FCSTD DOCUMENT  (FreeCAD 0.20R29603 (Git))
Label: NombresBoda
License: All rights reserved
LicenseURL: http://en.wikipedia.org/wiki/All_rights_reserved
objects: Part::Part2DObjectPython×37, Part::Extrusion×37, App::DocumentObjectGroup×26, Part::MultiFuse×25, Part::Box×17, Part::Fuse×3
note: 119 computed .brp shape members not serialized (recipe doc carries the construction recipe); baked Part::Feature solids carry a one-line shape summary decoded from their .brp

FEATURE [Part::Part2DObjectPython] ShapeString  # Draft 2D object (typed FeaturePython)
  FontFile = <userpath>/Desktop/Pacifico/Pacifico-Regular.ttf
  MakeFace = true
  Placement = pos=(11.57,0.12,0) rot=(0,0,1;0rad)
  Size = 16
  String = uli
  Tracking = 0
FEATURE [Part::Part2DObjectPython] ShapeString001  # Draft 2D object (typed FeaturePython)
  FontFile = <userpath>/Desktop/Pacifico/Pacifico-Regular.ttf
  MakeFace = true
  Placement = pos=(-4,0.7,0) rot=(0,0,1;0rad)
  Size = 16
  String = J
  Tracking = 0
FEATURE [Part::Extrusion] Extrude
  Base = -> ShapeString001
  Dir = (0,0,1)
  DirMode = 2
  FaceMakerClass = Part::FaceMakerBullseye
  LengthFwd = 3.5
  LengthRev = 0
  Solid = true
  Symmetric = false
FEATURE [Part::Extrusion] Extrude001
  Base = -> ShapeString
  Dir = (0,0,1)
  DirMode = 2
  FaceMakerClass = Part::FaceMakerBullseye
  LengthFwd = 3
  LengthRev = 0
  Solid = true
  Symmetric = false
FEATURE [Part::Box] Box001  label="Cubo001"
  AttacherType = Attacher::AttachEngine3D
  Height = 2.5
  Length = 2
  Placement = pos=(-8,-5,0) rot=(0,0,1;0rad)
  Width = 6
FEATURE [Part::Part2DObjectPython] ShapeString002  # Draft 2D object (typed FeaturePython)
  FontFile = <userpath>/Desktop/Pacifico/Pacifico-Regular.ttf
  MakeFace = true
  Placement = pos=(-1,0,0) rot=(0,0,1;0rad)
  Size = 16
  String = Raquel
  Tracking = 0
FEATURE [Part::Extrusion] Extrude002
  Base = -> ShapeString002
  Dir = (0,0,1)
  DirMode = 2
  FaceMakerClass = Part::FaceMakerBullseye
  LengthFwd = 3
  LengthRev = 0
  Solid = true
  Symmetric = false
FEATURE [App::DocumentObjectGroup] Group001  label="Raquel"
  Group = -> [Extrude002]
FEATURE [Part::Part2DObjectPython] ShapeString003  label="Base"  # Draft 2D object (typed FeaturePython)
  FontFile = <userpath>/Desktop/Pacifico/Pacifico-Regular.ttf
  MakeFace = true
  Placement = pos=(-1,0,0) rot=(0,0,1;0rad)
  Size = 16
  String = Rocio
  Tracking = 0
FEATURE [Part::Part2DObjectPython] ShapeString004  label="RocIo"  # Draft 2D object (typed FeaturePython)
  FontFile = <userpath>/Desktop/Pacifico/Pacifico-Regular.ttf
  MakeFace = true
  Placement = pos=(-1,0,0) rot=(0,0,1;0rad)
  Size = 16
  String = Rocio
  Tracking = 0
FEATURE [Part::Extrusion] Extrude003
  Base = -> ShapeString004
  Dir = (0,0,1)
  DirMode = 2
  FaceMakerClass = Part::FaceMakerBullseye
  LengthFwd = 3
  LengthRev = 0
  Solid = true
  Symmetric = false
FEATURE [Part::Box] Box002  label="Cubo002"
  AttacherType = Attacher::AttachEngine3D
  Height = 2
  Length = 1.5
  Placement = pos=(50.5,13,0) rot=(0,0,1;-0.174533rad)
  Width = 3
FEATURE [Part::Fuse] Fusion001
  Base = -> Extrude003
  Refine = true
  Tool = -> Box002
FEATURE [App::DocumentObjectGroup] Group002  label="Rocio"
  Group = -> [Fusion001]
FEATURE [Part::Box] Box003  label="Cubo003"
  AttacherType = Attacher::AttachEngine3D
  Height = 2
  Length = 1.5
  Placement = pos=(36.25,12,0) rot=(0,0,1;-0.174533rad)
  Width = 4
FEATURE [Part::Part2DObjectPython] ShapeString005  # Draft 2D object (typed FeaturePython)
  FontFile = <userpath>/Desktop/Pacifico/Pacifico-Regular.ttf
  MakeFace = true
  Placement = pos=(12,0,0) rot=(0,0,1;0rad)
  Size = 15
  String = ulio
  Tracking = 0
FEATURE [Part::Extrusion] Extrude005
  Base = -> ShapeString005
  Dir = (0,0,1)
  DirMode = 2
  FaceMakerClass = Part::FaceMakerBullseye
  LengthFwd = 3
  LengthRev = 0
  Solid = true
  Symmetric = false
FEATURE [Part::Part2DObjectPython] ShapeString006  # Draft 2D object (typed FeaturePython)
  FontFile = <userpath>/Desktop/Pacifico/Pacifico-Regular.ttf
  MakeFace = true
  Placement = pos=(-3,0.7,0) rot=(0,0,1;0rad)
  Size = 15
  String = J
  Tracking = 0
FEATURE [Part::Extrusion] Extrude004
  Base = -> ShapeString006
  Dir = (0,0,1)
  DirMode = 2
  FaceMakerClass = Part::FaceMakerBullseye
  LengthFwd = 3.5
  LengthRev = 0
  Solid = true
  Symmetric = false
FEATURE [Part::Fuse] Fusion002
  Base = -> Extrude004
  Refine = true
  Tool = -> Extrude005
FEATURE [Part::Box] Box004  label="Cubo004"
  AttacherType = Attacher::AttachEngine3D
  Height = 2.5
  Length = 1.5
  Placement = pos=(37.25,13,0) rot=(0,0,1;-0.174533rad)
  Width = 3
FEATURE [Part::Fuse] Fusion004
  Base = -> Box003
  Refine = true
  Tool = -> Fusion002
FEATURE [App::DocumentObjectGroup] Group003  label="Julio"
  Group = -> [Fusion004]
FEATURE [Part::Part2DObjectPython] ShapeString007  label="Base001"  # Draft 2D object (typed FeaturePython)
  FontFile = <userpath>/Desktop/Pacifico/Pacifico-Regular.ttf
  MakeFace = true
  Placement = pos=(-1,0,0) rot=(0,0,1;0rad)
  Size = 16
  String = Yolanda
  Tracking = 0
FEATURE [Part::Extrusion] Extrude006
  Base = -> ShapeString007
  Dir = (0,0,1)
  DirMode = 2
  FaceMakerClass = Part::FaceMakerBullseye
  LengthFwd = 3
  LengthRev = 0
  Solid = true
  Symmetric = false
FEATURE [App::DocumentObjectGroup] Group004  label="Yolanda"
  Group = -> [Extrude006]
FEATURE [Part::Part2DObjectPython] ShapeString008  label="Base002"  # Draft 2D object (typed FeaturePython)
  FontFile = <userpath>/Desktop/Pacifico/Pacifico-Regular.ttf
  MakeFace = true
  Placement = pos=(-1,0,0) rot=(0,0,1;0rad)
  Size = 16
  String = Marcos
  Tracking = 0
FEATURE [Part::Extrusion] Extrude007
  Base = -> ShapeString008
  Dir = (0,0,1)
  DirMode = 2
  FaceMakerClass = Part::FaceMakerBullseye
  LengthFwd = 3
  LengthRev = 0
  Solid = true
  Symmetric = false
FEATURE [App::DocumentObjectGroup] Group005  label="Marco"
  Group = -> [Extrude007]
FEATURE [Part::MultiFuse] Fusion
  Refine = true
  Shapes = -> [Extrude,Extrude001]
FEATURE [Part::MultiFuse] Fusion005
  Refine = true
  Shapes = -> [Fusion,Box004]
FEATURE [App::DocumentObjectGroup] Group  label="Juli"
  Group = -> [Fusion005]
FEATURE [Part::Part2DObjectPython] ShapeString009  label="Base003"  # Draft 2D object (typed FeaturePython)
  FontFile = <userpath>/Desktop/Pacifico/Pacifico-Regular.ttf
  MakeFace = true
  Placement = pos=(23,0,0) rot=(0,0,1;0rad)
  Size = 16
  String = esus
  Tracking = 0
FEATURE [Part::Part2DObjectPython] ShapeString010  label="Base004"  # Draft 2D object (typed FeaturePython)
  FontFile = <userpath>/Desktop/Pacifico/Pacifico-Regular.ttf
  MakeFace = true
  Placement = pos=(7,0,0) rot=(0,0,1;0rad)
  Size = 16
  String = J
  Tracking = 0
FEATURE [Part::Part2DObjectPython] ShapeString011  label="Base005"  # Draft 2D object (typed FeaturePython)
  FontFile = <userpath>/Desktop/Pacifico/Pacifico-Regular.ttf
  MakeFace = true
  Placement = pos=(-32,0,0) rot=(0,0,1;0rad)
  Size = 16
  String = M
  Tracking = 0
FEATURE [Part::Part2DObjectPython] ShapeString012  label="Base006"  # Draft 2D object (typed FeaturePython)
  FontFile = <userpath>/Desktop/Pacifico/Pacifico-Regular.ttf
  MakeFace = true
  Placement = pos=(-2,0,0) rot=(0,0,1;0rad)
  Size = 16
  String = ª
  Tracking = 0
FEATURE [Part::Extrusion] Extrude008
  Base = -> ShapeString009
  Dir = (0,0,1)
  DirMode = 2
  FaceMakerClass = Part::FaceMakerBullseye
  LengthFwd = 3
  LengthRev = 0
  Solid = true
  Symmetric = false
FEATURE [Part::Extrusion] Extrude009
  Base = -> ShapeString010
  Dir = (0,0,1)
  DirMode = 2
  FaceMakerClass = Part::FaceMakerBullseye
  LengthFwd = 3
  LengthRev = 0
  Solid = true
  Symmetric = false
FEATURE [Part::Extrusion] Extrude010
  Base = -> ShapeString011
  Dir = (0,0,1)
  DirMode = 2
  FaceMakerClass = Part::FaceMakerBullseye
  LengthFwd = 3
  LengthRev = 0
  Solid = true
  Symmetric = false
FEATURE [Part::Extrusion] Extrude011
  Base = -> ShapeString012
  Dir = (0,0,1)
  DirMode = 2
  FaceMakerClass = Part::FaceMakerBullseye
  LengthFwd = 2.5
  LengthRev = 0
  Solid = true
  Symmetric = false
FEATURE [Part::MultiFuse] Fusion006
  Refine = true
  Shapes = -> [Extrude008,Extrude009]
FEATURE [Part::MultiFuse] Fusion007
  Refine = true
  Shapes = -> [Fusion006,Extrude011]
FEATURE [Part::MultiFuse] Fusion008
  Refine = true
  Shapes = -> [Extrude010,Fusion007]
FEATURE [App::DocumentObjectGroup] Group006  label="MJesus"
  Group = -> [ShapeString009,ShapeString010,ShapeString011,ShapeString012,Fusion008]
FEATURE [Part::Part2DObjectPython] ShapeString013  label="Base007"  # Draft 2D object (typed FeaturePython)
  FontFile = <userpath>/Desktop/Pacifico/Pacifico-Regular.ttf
  MakeFace = true
  Placement = pos=(-1,0,0) rot=(0,0,1;0rad)
  Size = 20
  String = Uti
  Tracking = 0
FEATURE [Part::Box] Box  label="Cubo"
  AttacherType = Attacher::AttachEngine3D
  Height = 2.5
  Length = 2
  Placement = pos=(49,16,0) rot=(0,0,1;-0.05236rad)
  Width = 4
FEATURE [Part::Extrusion] Extrude012
  Base = -> ShapeString013
  Dir = (0,0,1)
  DirMode = 2
  FaceMakerClass = Part::FaceMakerBullseye
  LengthFwd = 3
  LengthRev = 0
  Solid = true
  Symmetric = false
FEATURE [Part::MultiFuse] Fusion009
  Refine = true
  Shapes = -> [Box,Extrude012]
FEATURE [App::DocumentObjectGroup] Group007  label="Uti"
  Group = -> [Fusion009]
FEATURE [Part::Part2DObjectPython] ShapeString014  label="Base008"  # Draft 2D object (typed FeaturePython)
  FontFile = <userpath>/Desktop/Pacifico/Pacifico-Regular.ttf
  MakeFace = true
  Placement = pos=(15,0,0) rot=(0,0,1;0rad)
  Size = 16
  String = uani
  Tracking = 0
FEATURE [Part::Box] Box005  label="Cubo005"
  AttacherType = Attacher::AttachEngine3D
  Height = 2
  Length = 2
  Placement = pos=(58.5,12,0) rot=(0,0,1;-0.15708rad)
  Width = 4
FEATURE [Part::Extrusion] Extrude013
  Base = -> ShapeString014
  Dir = (0,0,1)
  DirMode = 2
  FaceMakerClass = Part::FaceMakerBullseye
  LengthFwd = 3
  LengthRev = 0
  Solid = true
  Symmetric = false
FEATURE [Part::Extrusion] Extrude014  label="Base009"
  Base = -> ShapeString003
  Dir = (0,0,1)
  DirMode = 2
  FaceMakerClass = Part::FaceMakerBullseye
  LengthFwd = 3
  LengthRev = 0
  Solid = true
  Symmetric = false
FEATURE [Part::Part2DObjectPython] ShapeString015  label="Base011"  # Draft 2D object (typed FeaturePython)
  FontFile = <userpath>/Desktop/Pacifico/Pacifico-Regular.ttf
  MakeFace = true
  Placement = pos=(-1,0,0) rot=(0,0,1;0rad)
  Size = 16
  String = J
  Tracking = 0
FEATURE [Part::Extrusion] Extrude015  label="Base010"
  Base = -> ShapeString015
  Dir = (0,0,1)
  DirMode = 2
  FaceMakerClass = Part::FaceMakerBullseye
  LengthFwd = 3
  LengthRev = 0
  Solid = true
  Symmetric = false
FEATURE [Part::MultiFuse] Fusion010
  Refine = true
  Shapes = -> [Extrude013,Extrude015]
FEATURE [Part::MultiFuse] Fusion011
  Refine = true
  Shapes = -> [Fusion010,Box005]
FEATURE [App::DocumentObjectGroup] Group008  label="Juani"
  Group = -> [Fusion011]
FEATURE [Part::Part2DObjectPython] ShapeString016  label="Base013"  # Draft 2D object (typed FeaturePython)
  FontFile = <userpath>/Desktop/Pacifico/Pacifico-Regular.ttf
  MakeFace = true
  Placement = pos=(-1,0,0) rot=(0,0,1;0rad)
  Size = 16
  String = Alberto
  Tracking = 0
FEATURE [Part::Extrusion] Extrude016  label="Base012"
  Base = -> ShapeString016
  Dir = (0,0,1)
  DirMode = 2
  FaceMakerClass = Part::FaceMakerBullseye
  LengthFwd = 3
  LengthRev = 0
  Solid = true
  Symmetric = false
FEATURE [App::DocumentObjectGroup] Group009  label="Alberto"
  Group = -> [Extrude016]
FEATURE [Part::Part2DObjectPython] ShapeString017  label="Base015"  # Draft 2D object (typed FeaturePython)
  FontFile = <userpath>/Desktop/Pacifico/Pacifico-Regular.ttf
  MakeFace = true
  Placement = pos=(-1,0,0) rot=(0,0,1;0rad)
  Size = 16
  String = aime
  Tracking = 0
FEATURE [Part::Extrusion] Extrude017  label="Base014"
  Base = -> ShapeString017
  Dir = (0,0,1)
  DirMode = 2
  FaceMakerClass = Part::FaceMakerBullseye
  LengthFwd = 3
  LengthRev = 0
  Solid = true
  Symmetric = false
FEATURE [Part::Part2DObjectPython] ShapeString018  label="Base016"  # Draft 2D object (typed FeaturePython)
  FontFile = <userpath>/Desktop/Pacifico/Pacifico-Regular.ttf
  MakeFace = true
  Placement = pos=(-17,0,0) rot=(0,0,1;0rad)
  Size = 16
  String = J
  Tracking = 0
FEATURE [Part::Extrusion] Extrude018
  Base = -> ShapeString018
  Dir = (0,0,1)
  DirMode = 2
  FaceMakerClass = Part::FaceMakerBullseye
  LengthFwd = 3
  LengthRev = 0
  Solid = true
  Symmetric = false
FEATURE [Part::MultiFuse] Fusion012
  Refine = true
  Shapes = -> [Extrude017,Extrude018]
FEATURE [Part::Box] Box006  label="Cubo006"
  AttacherType = Attacher::AttachEngine3D
  Height = 2
  Length = 2
  Placement = pos=(16,12,0) rot=(0,0,1;-0.10472rad)
  Width = 4
FEATURE [Part::MultiFuse] Fusion013
  Refine = true
  Shapes = -> [Box006,Fusion012]
FEATURE [App::DocumentObjectGroup] Group010  label="Jaime"
  Group = -> [Fusion013]
FEATURE [Part::Part2DObjectPython] ShapeString019  label="Base018"  # Draft 2D object (typed FeaturePython)
  FontFile = <userpath>/Desktop/Pacifico/Pacifico-Regular.ttf
  MakeFace = true
  Placement = pos=(-1,0,0) rot=(0,0,1;0rad)
  Size = 16
  String = Antonio
  Tracking = 0
FEATURE [Part::Extrusion] Extrude019  label="Base017"
  Base = -> ShapeString019
  Dir = (0,0,1)
  DirMode = 2
  FaceMakerClass = Part::FaceMakerBullseye
  LengthFwd = 3
  LengthRev = 0
  Solid = true
  Symmetric = false
FEATURE [Part::Box] Box007  label="Cubo007"
  AttacherType = Attacher::AttachEngine3D
  Height = 2
  Length = 2
  Placement = pos=(76.3,12,0) rot=(0,0,1;-0.174533rad)
  Width = 5
FEATURE [Part::MultiFuse] Fusion014
  Refine = true
  Shapes = -> [Extrude019,Box007]
FEATURE [App::DocumentObjectGroup] Group011  label="Antonio"
  Group = -> [Fusion014]
FEATURE [Part::Part2DObjectPython] ShapeString020  label="Base020"  # Draft 2D object (typed FeaturePython)
  FontFile = <userpath>/Desktop/Pacifico/Pacifico-Regular.ttf
  MakeFace = true
  Placement = pos=(-1,0,0) rot=(0,0,1;0rad)
  Size = 16
  String = Esme
  Tracking = 0
FEATURE [Part::Extrusion] Extrude020  label="Base019"
  Base = -> ShapeString020
  Dir = (0,0,1)
  DirMode = 2
  FaceMakerClass = Part::FaceMakerBullseye
  LengthFwd = 3
  LengthRev = 0
  Solid = true
  Symmetric = false
FEATURE [App::DocumentObjectGroup] Group012  label="Esme"
  Group = -> [Extrude020]
FEATURE [Part::Part2DObjectPython] ShapeString021  label="Base022"  # Draft 2D object (typed FeaturePython)
  FontFile = <userpath>/Desktop/Pacifico/Pacifico-Regular.ttf
  MakeFace = true
  Placement = pos=(15,0,0) rot=(0,0,1;0rad)
  Size = 16
  String = avi
  Tracking = 0
FEATURE [Part::Extrusion] Extrude021  label="Base021"
  Base = -> ShapeString021
  Dir = (0,0,1)
  DirMode = 2
  FaceMakerClass = Part::FaceMakerBullseye
  LengthFwd = 3
  LengthRev = 0
  Solid = true
  Symmetric = false
FEATURE [Part::Part2DObjectPython] ShapeString022  label="Base023"  # Draft 2D object (typed FeaturePython)
  FontFile = <userpath>/Desktop/Pacifico/Pacifico-Regular.ttf
  MakeFace = true
  Placement = pos=(-1,0,0) rot=(0,0,1;0rad)
  Size = 16
  String = J
  Tracking = 0
FEATURE [Part::Extrusion] Extrude022
  Base = -> ShapeString022
  Dir = (0,0,1)
  DirMode = 2
  FaceMakerClass = Part::FaceMakerBullseye
  LengthFwd = 3
  LengthRev = 0
  Solid = true
  Symmetric = false
FEATURE [Part::MultiFuse] Fusion015
  Refine = true
  Shapes = -> [Extrude021,Extrude022]
FEATURE [Part::Box] Box008  label="Cubo008"
  AttacherType = Attacher::AttachEngine3D
  Height = 2
  Length = 2
  Placement = pos=(44.7,12,0) rot=(0,0,1;-0.122173rad)
  Width = 6
FEATURE [Part::MultiFuse] Fusion016
  Refine = true
  Shapes = -> [Fusion015,Box008]
FEATURE [App::DocumentObjectGroup] Group013  label="Javi"
  Group = -> [Fusion016]
FEATURE [Part::Part2DObjectPython] ShapeString023  label="Base025"  # Draft 2D object (typed FeaturePython)
  FontFile = <userpath>/Desktop/Pacifico/Pacifico-Regular.ttf
  MakeFace = true
  Placement = pos=(-1,0,0) rot=(0,0,1;0rad)
  Size = 16
  String = Maxi
  Tracking = 0
FEATURE [Part::Extrusion] Extrude023  label="Base024"
  Base = -> ShapeString023
  Dir = (0,0,1)
  DirMode = 2
  FaceMakerClass = Part::FaceMakerBullseye
  LengthFwd = 3
  LengthRev = 0
  Solid = true
  Symmetric = false
FEATURE [Part::Box] Box009  label="Cubo009"
  AttacherType = Attacher::AttachEngine3D
  Height = 2
  Length = 2
  Placement = pos=(64.7,12,0) rot=(0,0,1;-0.139626rad)
  Width = 6
FEATURE [Part::MultiFuse] Fusion017
  Refine = true
  Shapes = -> [Extrude023,Box009]
FEATURE [App::DocumentObjectGroup] Group014  label="Maxi"
  Group = -> [Fusion017]
FEATURE [Part::Part2DObjectPython] ShapeString024  label="Base027"  # Draft 2D object (typed FeaturePython)
  FontFile = <userpath>/Desktop/Pacifico/Pacifico-Regular.ttf
  MakeFace = true
  Placement = pos=(-1,0,0) rot=(0,0,1;0rad)
  Size = 16
  String = Araceli
  Tracking = 0
FEATURE [Part::Extrusion] Extrude024  label="Base026"
  Base = -> ShapeString024
  Dir = (0,0,1)
  DirMode = 2
  FaceMakerClass = Part::FaceMakerBullseye
  LengthFwd = 3
  LengthRev = 0
  Solid = true
  Symmetric = false
FEATURE [Part::Box] Box010  label="Cubo010"
  AttacherType = Attacher::AttachEngine3D
  Height = 2
  Length = 2
  Placement = pos=(81.7,12,0) rot=(0,0,1;-0.15708rad)
  Width = 6
FEATURE [Part::MultiFuse] Fusion018
  Refine = true
  Shapes = -> [Extrude024,Box010]
FEATURE [App::DocumentObjectGroup] Group015  label="Araceli"
  Group = -> [Fusion018]
FEATURE [Part::Part2DObjectPython] ShapeString025  label="Base029"  # Draft 2D object (typed FeaturePython)
  FontFile = <userpath>/Desktop/Pacifico/Pacifico-Regular.ttf
  MakeFace = true
  Placement = pos=(-1,0,0) rot=(0,0,1;0rad)
  Size = 16
  String = Adri
  Tracking = 0
FEATURE [Part::Extrusion] Extrude025  label="Base028"
  Base = -> ShapeString025
  Dir = (0,0,1)
  DirMode = 2
  FaceMakerClass = Part::FaceMakerBullseye
  LengthFwd = 3
  LengthRev = 0
  Solid = true
  Symmetric = false
FEATURE [Part::Box] Box011  label="Cubo011"
  AttacherType = Attacher::AttachEngine3D
  Height = 2
  Length = 2
  Placement = pos=(52,13,0) rot=(0,0,1;-0.139626rad)
  Width = 6
FEATURE [Part::MultiFuse] Fusion019
  Refine = true
  Shapes = -> [Box011,Extrude025]
FEATURE [App::DocumentObjectGroup] Group016  label="Adri"
  Group = -> [Fusion019]
FEATURE [Part::Part2DObjectPython] ShapeString026  label="Base031"  # Draft 2D object (typed FeaturePython)
  FontFile = <userpath>/Desktop/Pacifico/Pacifico-Regular.ttf
  MakeFace = true
  Placement = pos=(15.6,0,0) rot=(0,0,1;0rad)
  Size = 16
  String = eila
  Tracking = 0
FEATURE [Part::Extrusion] Extrude026  label="Base030"
  Base = -> ShapeString026
  Dir = (0,0,1)
  DirMode = 2
  FaceMakerClass = Part::FaceMakerBullseye
  LengthFwd = 3
  LengthRev = 0
  Solid = true
  Symmetric = false
FEATURE [Part::Part2DObjectPython] ShapeString027  label="Base033"  # Draft 2D object (typed FeaturePython)
  FontFile = <userpath>/Desktop/Pacifico/Pacifico-Regular.ttf
  MakeFace = true
  Placement = pos=(-1,0,0) rot=(0,0,1;0rad)
  Size = 16
  String = S
  Tracking = 0
FEATURE [Part::Extrusion] Extrude027  label="Base032"
  Base = -> ShapeString027
  Dir = (0,0,1)
  DirMode = 2
  FaceMakerClass = Part::FaceMakerBullseye
  LengthFwd = 3
  LengthRev = 0
  Solid = true
  Symmetric = false
FEATURE [Part::MultiFuse] Fusion020
  Refine = true
  Shapes = -> [Extrude026,Extrude027]
FEATURE [Part::Box] Box012  label="Cubo012"
  AttacherType = Attacher::AttachEngine3D
  Height = 2
  Length = 2
  Placement = pos=(29.7,11,0) rot=(0,0,1;-0.15708rad)
  Width = 6
FEATURE [Part::MultiFuse] Fusion021
  Refine = true
  Shapes = -> [Fusion020,Box012]
FEATURE [App::DocumentObjectGroup] Group017  label="Seila"
  Group = -> [Fusion021]
FEATURE [Part::Part2DObjectPython] ShapeString028  label="Base035"  # Draft 2D object (typed FeaturePython)
  FontFile = <userpath>/Desktop/Pacifico/Pacifico-Regular.ttf
  MakeFace = true
  Placement = pos=(12,0,0) rot=(0,0,1;0rad)
  Size = 16
  String = uan
  Tracking = 0
FEATURE [Part::Extrusion] Extrude028  label="Base034"
  Base = -> ShapeString028
  Dir = (0,0,1)
  DirMode = 2
  FaceMakerClass = Part::FaceMakerBullseye
  LengthFwd = 3
  LengthRev = 0
  Solid = true
  Symmetric = false
FEATURE [Part::Part2DObjectPython] ShapeString029  label="Base037"  # Draft 2D object (typed FeaturePython)
  FontFile = <userpath>/Desktop/Pacifico/Pacifico-Regular.ttf
  MakeFace = true
  Placement = pos=(-1,0,0) rot=(0,0,1;0rad)
  Size = 16
  String = David
  Tracking = 0
FEATURE [Part::Extrusion] Extrude029  label="Base036"
  Base = -> ShapeString029
  Dir = (0,0,1)
  DirMode = 2
  FaceMakerClass = Part::FaceMakerBullseye
  LengthFwd = 3
  LengthRev = 0
  Placement = pos=(-1,4,0) rot=(0,0,1;0rad)
  Solid = true
  Symmetric = false
FEATURE [App::DocumentObjectGroup] Group019  label="Novios"
  Group = -> [Group,Group003,Group006,Group002]
FEATURE [Part::Part2DObjectPython] ShapeString030  # Draft 2D object (typed FeaturePython)
  FontFile = <userpath>/Desktop/Pacifico/Pacifico-Regular.ttf
  MakeFace = true
  Placement = pos=(-3.1,2.29,0) rot=(0,0,1;0rad)
  Size = 16
  String = J
  Tracking = 0
FEATURE [Part::Extrusion] Extrude030
  Base = -> ShapeString030
  Dir = (0,0,1)
  DirMode = 2
  FaceMakerClass = Part::FaceMakerBullseye
  LengthFwd = 3
  LengthRev = 0
  Solid = true
  Symmetric = false
FEATURE [Part::MultiFuse] Fusion022
  Refine = true
  Shapes = -> [Extrude028,Extrude030]
FEATURE [App::DocumentObjectGroup] Group020  label="Juan"
  Group = -> [Fusion022]
FEATURE [Part::Part2DObjectPython] ShapeString031  label="Base039"  # Draft 2D object (typed FeaturePython)
  FontFile = <userpath>/Desktop/Pacifico/Pacifico-Regular.ttf
  MakeFace = true
  Placement = pos=(-1,0,0) rot=(0,0,1;0rad)
  Size = 16
  String = Noé
  Tracking = 0
FEATURE [Part::Extrusion] Extrude031  label="Base038"
  Base = -> ShapeString031
  Dir = (0,0,1)
  DirMode = 2
  FaceMakerClass = Part::FaceMakerBullseye
  LengthFwd = 3
  LengthRev = 0
  Solid = true
  Symmetric = false
FEATURE [Part::Box] Box013  label="Cubo013"
  AttacherType = Attacher::AttachEngine3D
  Height = 2.5
  Length = 1.5
  Placement = pos=(44,11,0) rot=(0,0,1;0rad)
  Width = 6
FEATURE [Part::MultiFuse] Fusion023
  Refine = true
  Shapes = -> [Extrude031,Box013]
FEATURE [App::DocumentObjectGroup] Group021  label="Noe"
  Group = -> [Fusion023]
FEATURE [Part::Part2DObjectPython] ShapeString032  label="Base041"  # Draft 2D object (typed FeaturePython)
  FontFile = <userpath>/Desktop/Pacifico/Pacifico-Regular.ttf
  MakeFace = true
  Placement = pos=(-1,0,0) rot=(0,0,1;0rad)
  Size = 16
  String = Rebeca
  Tracking = 0
FEATURE [Part::Extrusion] Extrude032  label="Base040"
  Base = -> ShapeString032
  Dir = (0,0,1)
  DirMode = 2
  FaceMakerClass = Part::FaceMakerBullseye
  LengthFwd = 3
  LengthRev = 0
  Solid = true
  Symmetric = false
FEATURE [App::DocumentObjectGroup] Group022  label="Rebeca"
  Group = -> [Extrude032]
FEATURE [Part::Part2DObjectPython] ShapeString033  label="Base043"  # Draft 2D object (typed FeaturePython)
  FontFile = <userpath>/Desktop/Pacifico/Pacifico-Regular.ttf
  MakeFace = true
  Placement = pos=(-1,0,0) rot=(0,0,1;0rad)
  Size = 16
  String = Mamen
  Tracking = 0
FEATURE [Part::Extrusion] Extrude033  label="Base042"
  Base = -> ShapeString033
  Dir = (0,0,1)
  DirMode = 2
  FaceMakerClass = Part::FaceMakerBullseye
  LengthFwd = 3
  LengthRev = 0
  Solid = true
  Symmetric = false
FEATURE [App::DocumentObjectGroup] Group023  label="Mamen"
  Group = -> [Extrude033]
FEATURE [Part::Part2DObjectPython] ShapeString034  label="Base045"  # Draft 2D object (typed FeaturePython)
  FontFile = <userpath>/Desktop/Pacifico/Pacifico-Regular.ttf
  MakeFace = true
  Placement = pos=(-1,0,0) rot=(0,0,1;0rad)
  Size = 16
  String = Chino
  Tracking = 0
FEATURE [Part::Extrusion] Extrude034  label="Base044"
  Base = -> ShapeString034
  Dir = (0,0,1)
  DirMode = 2
  FaceMakerClass = Part::FaceMakerBullseye
  LengthFwd = 3
  LengthRev = 0
  Placement = pos=(0,-19,0) rot=(0,0,1;0rad)
  Solid = true
  Symmetric = false
FEATURE [Part::MultiFuse] Fusion024
  Refine = true
  Shapes = -> [Extrude034,Extrude029]
FEATURE [Part::Box] Box014  label="Cubo014"
  AttacherType = Attacher::AttachEngine3D
  Height = 2.5
  Length = 2
  Placement = pos=(51,15,0) rot=(0,0,1;-0.10472rad)
  Width = 6
FEATURE [Part::MultiFuse] Fusion025
  Refine = true
  Shapes = -> [Fusion024,Box014]
FEATURE [Part::Box] Box015  label="Cubo015"
  AttacherType = Attacher::AttachEngine3D
  Height = 2.5
  Length = 2
  Placement = pos=(35.7,-7,0) rot=(0,0,1;-0.10472rad)
  Width = 6
FEATURE [Part::MultiFuse] Fusion026
  Refine = true
  Shapes = -> [Box015,Fusion025]
FEATURE [App::DocumentObjectGroup] Group024  label="DavidChino"
  Group = -> [Fusion026]
FEATURE [Part::Part2DObjectPython] ShapeString035  label="Base047"  # Draft 2D object (typed FeaturePython)
  FontFile = <userpath>/Desktop/Pacifico/Pacifico-Regular.ttf
  MakeFace = true
  Placement = pos=(11,0,0) rot=(0,0,1;0rad)
  Size = 16
  String = ania
  Tracking = 0
FEATURE [Part::Extrusion] Extrude035  label="Base046"
  Base = -> ShapeString035
  Dir = (0,0,1)
  DirMode = 2
  FaceMakerClass = Part::FaceMakerBullseye
  LengthFwd = 3
  LengthRev = 0
  Solid = true
  Symmetric = false
FEATURE [Part::Part2DObjectPython] ShapeString036  # Draft 2D object (typed FeaturePython)
  FontFile = <userpath>/Desktop/Pacifico/Pacifico-Regular.ttf
  MakeFace = true
  Size = 16
  String = T
  Tracking = 0
FEATURE [Part::Extrusion] Extrude036
  Base = -> ShapeString036
  Dir = (0,0,1)
  DirMode = 2
  FaceMakerClass = Part::FaceMakerBullseye
  LengthFwd = 3
  LengthRev = 0
  Solid = true
  Symmetric = false
FEATURE [Part::MultiFuse] Fusion027
  Refine = true
  Shapes = -> [Extrude035,Extrude036]
FEATURE [Part::Box] Box016  label="Cubo016"
  AttacherType = Attacher::AttachEngine3D
  Height = 2.5
  Length = 2
  Placement = pos=(41.7,10,0) rot=(0,0,1;-0.10472rad)
  Width = 6
FEATURE [Part::MultiFuse] Fusion028
  Refine = true
  Shapes = -> [Box016,Fusion027]
FEATURE [App::DocumentObjectGroup] Group025  label="Tania"
  Group = -> [Fusion028]
FEATURE [App::DocumentObjectGroup] Group018  label="Hechos"
  Group = -> [Group016,Group011,Group015,Group012,Group010,Group013,Group008,Group005,Group014,Group001,Group017,Group009,Group007,Group004,Group020,Group021,Group022,Group023,Group024,Group025]
